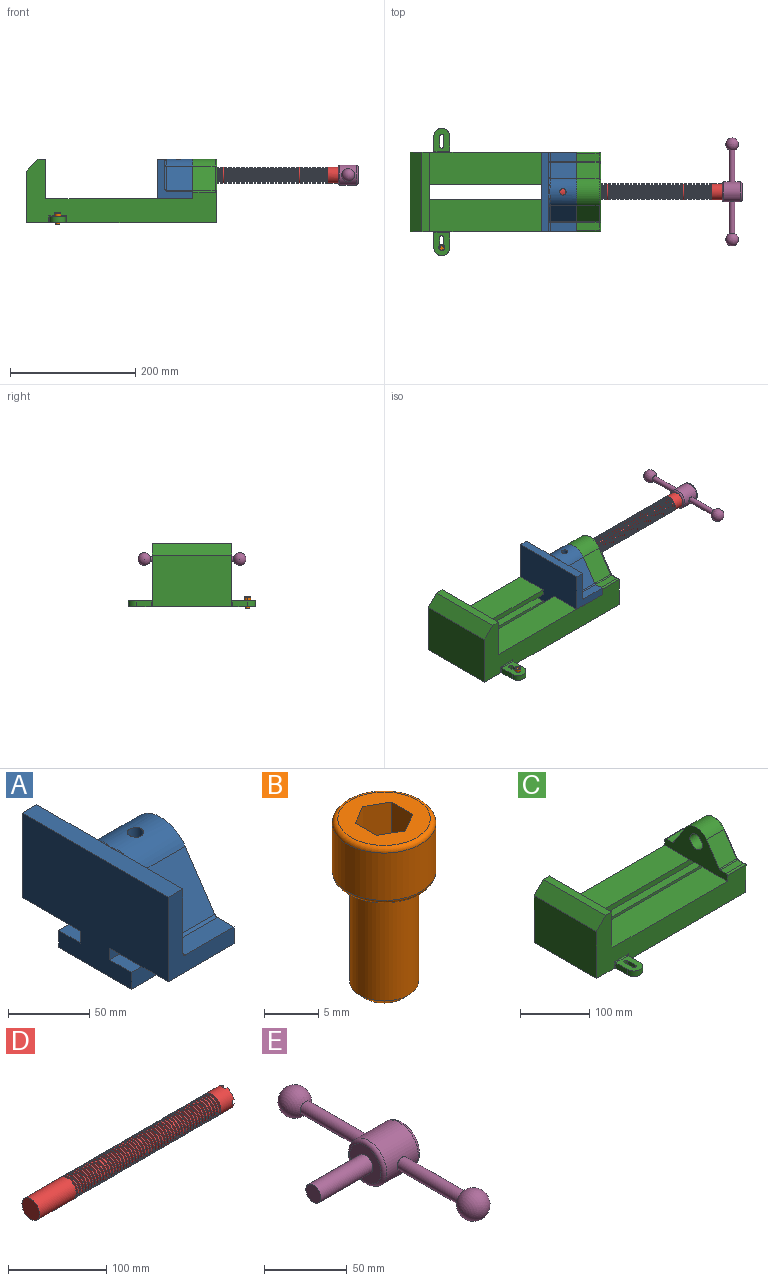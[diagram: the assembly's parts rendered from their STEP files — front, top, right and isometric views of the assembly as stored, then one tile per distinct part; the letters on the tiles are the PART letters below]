
ASSEMBLY  parts=5 mates=5
PART A: 36 faces, bbox 57.2x127x89 mm
  f0: plane 57.15x50.8mm, normal (0,0,-1), area 2903.2mm2, adj f6,f9,f10,f23
  f1: cylinder r=12.7mm len=44.45mm, axis (1,0,0), area 3464.3mm2, adj f6,f15,f16
  f2: plane 41.91x14.52mm, normal (0,0,1), area 608.5mm2, adj f6,f11,f24,f25
  f3: plane 51.86x48.26mm, normal (1,0,0), area 1495.7mm2, adj f8,f10,f31,f33,f35
  f4: plane 51.86x48.26mm, normal (1,0,0), area 1495.7mm2, adj f8,f11,f24,f28,f29
  f5: plane 57.15x50.8mm, normal (0,0,-1), area 2903.2mm2, adj f6,f9,f11,f22
  f6: plane 127x85.09mm, normal (1,0,0), area 5190.6mm2, adj f0,f1,f2,f5,f7,f10,f11,f12
  f7: plane 41.91x14.52mm, normal (0,0,1), area 608.5mm2, adj f6,f10,f30,f31
  f8: plane 127x12.7mm, normal (0,0,1), area 1612.9mm2, adj f3,f4,f9,f10,f11,f26,f34
  f9: plane 127x85.09mm, normal (-1,0,0), area 9096.8mm2, adj f0,f5,f8,f10,f11,f17,f18,f19
  f10: plane 63.5x57.15mm, normal (0,-1,0), area 1372.3mm2, adj f0,f3,f6,f7,f8,f9,f31
  f11: plane 63.5x57.15mm, normal (0,1,0), area 1372.3mm2, adj f2,f4,f5,f6,f8,f9,f24
  f12: plane 41.91x38.43mm, normal (0,-0.83,0.56), area 1939.2mm2, adj f6,f13,f30,f33
  f13: cylinder r=25.4mm len=44.45mm, axis (1,0,0), area 2026.5mm2, adj f6,f12,f14,f16,f26,f28,f34,f35
  f14: plane 41.91x38.43mm, normal (0,0.83,0.56), area 1939.2mm2, adj f6,f13,f25,f29
  f15: plane 25.4x25.4mm, normal (1,0,0), area 506.7mm2, adj f1
  f16: cylinder r=5.08mm len=13.76mm, axis (0,0,1), area 414mm2, adj f1,f13
  f17: plane 57.15x19.05mm, normal (0,0,1), area 1088.7mm2, adj f6,f9,f18,f23
  f18: plane 57.15x12.7mm, normal (0,-1,0), area 725.8mm2, adj f6,f9,f17,f19
  f19: plane 63.5x57.15mm, normal (0,0,-1), area 3629mm2, adj f6,f9,f18,f20
  f20: plane 57.15x12.7mm, normal (0,1,0), area 725.8mm2, adj f6,f9,f19,f21
  f21: plane 57.15x19.05mm, normal (0,0,1), area 1088.7mm2, adj f6,f9,f20,f22
  f22: plane 57.15x8.89mm, normal (0,1,0), area 508.1mm2, adj f5,f6,f9,f21
  f23: plane 57.15x8.89mm, normal (0,-1,0), area 508.1mm2, adj f0,f6,f9,f17
  f24: cylinder r=2.54mm len=14.52mm, axis (0,-1,0), area 57.9mm2, adj f2,f4,f11,f27
  f25: cylinder r=2.54mm len=41.91mm, axis (1,0,0), area 104.3mm2, adj f2,f6,f14,f27
  f26: bspline ~12.24x2.8mm, area 20.9mm2, adj f8,f13,f28
  f27: sphere r=2.54mm, area 6.3mm2, adj f24,f25,f29
  f28: torus R=27.94mm, axis (1,0,0), area 57.8mm2, adj f4,f13,f26,f29
  f29: cylinder r=2.54mm len=39.84mm, axis (0,-0.56,0.83), area 184.6mm2, adj f4,f14,f27,f28
  f30: cylinder r=2.54mm len=41.91mm, axis (1,0,0), area 104.3mm2, adj f6,f7,f12,f32
  f31: cylinder r=2.54mm len=14.52mm, axis (0,-1,0), area 57.9mm2, adj f3,f7,f10,f32
  f32: sphere r=2.54mm, area 6.3mm2, adj f30,f31,f33
  f33: cylinder r=2.54mm len=39.84mm, axis (0,-0.56,-0.83), area 184.6mm2, adj f3,f12,f32,f35
  f34: bspline ~12.24x2.8mm, area 20.9mm2, adj f8,f13,f35
  f35: torus R=27.94mm, axis (1,0,0), area 57.8mm2, adj f3,f13,f33,f34
PART B: 15 faces, bbox 10.3x10.3x19.1 mm
  f0: plane 8.51x8.51mm, normal (0,0,1), area 37.2mm2, adj f5,f6,f7,f8,f9,f10,f14
  f1: cylinder r=3.17mm len=11.94mm, axis (0,0,1), area 238.2mm2, adj f4,f12
  f2: plane 4.83x4.83mm, normal (0,0,-1), area 18.3mm2, adj f12
  f3: cylinder r=4.76mm len=9.53mm, axis (0,0,-1), area 159.6mm2, adj f13,f14
  f4: plane 8.51x8.51mm, normal (0,0,-1), area 25.2mm2, adj f1,f13
  f5: plane 4.83x2.38mm, normal (-0.5,-0.87,0), area 13.3mm2, adj f0,f6,f10,f11
  f6: plane 4.83x2.38mm, normal (0.5,-0.87,0), area 13.3mm2, adj f0,f5,f7,f11
  f7: plane 4.83x2.75mm, normal (1,0,0), area 13.3mm2, adj f0,f6,f8,f11
  f8: plane 4.83x2.38mm, normal (0.5,0.87,0), area 13.3mm2, adj f0,f7,f9,f11
  f9: plane 4.83x2.38mm, normal (-0.5,0.87,0), area 13.3mm2, adj f0,f8,f10,f11
  f10: plane 4.83x2.75mm, normal (-1,0,0), area 13.3mm2, adj f0,f5,f9,f11
  f11: plane 5.5x4.76mm, normal (0,0,1), area 19.6mm2, adj f5,f6,f7,f8,f9,f10
  f12: cone r=3.17mm half-angle=45deg, axis (0,0,1), area 18.9mm2, adj f1,f2
  f13: torus R=4.25mm, axis (0,0,1), area 23mm2, adj f3,f4
  f14: torus R=4.25mm, axis (0,0,1), area 23mm2, adj f0,f3
PART C: 61 faces, bbox 304.8x203.2x103.7 mm
  f0: plane 304.8x101.6mm, normal (0,1,0), area 13520.3mm2, adj f3,f4,f5,f6,f7,f8,f9,f16
  f1: plane 304.8x101.6mm, normal (0,-1,0), area 13520.3mm2, adj f2,f3,f5,f6,f7,f8,f9,f16
  f2: plane 234.95x50.8mm, normal (0,0,1), area 11935.5mm2, adj f1,f5,f16,f26
  f3: plane 127x99.06mm, normal (1,0,0), area 7097.5mm2, adj f0,f1,f9,f14,f17,f18,f19,f20
  f4: plane 234.95x50.8mm, normal (0,0,1), area 11935.5mm2, adj f0,f5,f16,f27
  f5: plane 127x101.6mm, normal (1,0,0), area 9516.1mm2, adj f0,f1,f2,f4,f6,f9,f18,f19
  f6: plane 127x12.7mm, normal (0,0,1), area 1612.9mm2, adj f0,f1,f5,f7
  f7: plane 127x19.05mm, normal (-0.71,0,0.71), area 3421.5mm2, adj f0,f1,f6,f8
  f8: plane 127x82.55mm, normal (-1,0,0), area 10483.8mm2, adj f0,f1,f7,f9
  f9: plane 304.8x203.2mm, normal (0,0,-1), area 33298.3mm2, adj f0,f1,f3,f5,f8,f21,f22,f39
  f10: plane 35.56x11.98mm, normal (0,0,1), area 426mm2, adj f16,f28,f29,f30
  f11: plane 38.43x35.56mm, normal (0,0.83,0.56), area 1645.4mm2, adj f12,f16,f29,f32
  f12: cylinder r=25.4mm len=42.19mm, axis (1,0,0), area 1770.2mm2, adj f11,f13,f16,f33
  f13: plane 38.43x35.56mm, normal (0,-0.83,0.56), area 1645.4mm2, adj f12,f16,f34,f35
  f14: cylinder r=12.7mm len=38.1mm, axis (1,0,0), area 3040.2mm2, adj f3,f16
  f15: plane 35.56x11.98mm, normal (0,0,1), area 426mm2, adj f16,f34,f36,f38
  f16: plane 127x63.5mm, normal (-1,0,0), area 4155.5mm2, adj f0,f1,f2,f4,f10,f11,f12,f13
  f17: plane 38.1x25.4mm, normal (0,0,-1), area 967.7mm2, adj f3,f16,f26,f27
  f18: plane 273.05x19.05mm, normal (0,0,-1), area 5201.6mm2, adj f3,f5,f19,f26
  f19: plane 273.05x12.7mm, normal (0,1,0), area 3467.7mm2, adj f3,f5,f18,f20
  f20: plane 273.05x19.05mm, normal (0,0,1), area 5201.6mm2, adj f3,f5,f19,f21
  f21: plane 273.05x16.51mm, normal (0,1,0), area 4508.1mm2, adj f3,f5,f9,f20
  f22: plane 273.05x16.51mm, normal (0,-1,0), area 4508.1mm2, adj f3,f5,f9,f23
  f23: plane 273.05x19.05mm, normal (0,0,1), area 5201.6mm2, adj f3,f5,f22,f24
  f24: plane 273.05x12.7mm, normal (0,-1,0), area 3467.7mm2, adj f3,f5,f23,f25
  f25: plane 273.05x19.05mm, normal (0,0,-1), area 5201.6mm2, adj f3,f5,f24,f27
  f26: plane 273.05x8.89mm, normal (0,1,0), area 2427.4mm2, adj f2,f3,f5,f17,f18
  f27: plane 273.05x8.89mm, normal (0,-1,0), area 2427.4mm2, adj f3,f4,f5,f17,f25
  f28: cylinder r=2.54mm len=38.1mm, axis (1,0,0), area 148.3mm2, adj f0,f10,f16,f30
  f29: cylinder r=2.54mm len=35.56mm, axis (-1,0,0), area 88.5mm2, adj f10,f11,f16,f31
  f30: cylinder r=2.54mm len=14.52mm, axis (0,1,0), area 54.3mm2, adj f3,f10,f28,f31
  f31: torus R=5.08mm, axis (-1,0,0), area 13.5mm2, adj f3,f29,f30,f32
  f32: cylinder r=2.54mm len=39.84mm, axis (0,0.56,-0.83), area 184.6mm2, adj f3,f11,f31,f33
  f33: torus R=22.86mm, axis (-1,0,0), area 191.4mm2, adj f3,f12,f32,f35
  f34: cylinder r=2.54mm len=35.56mm, axis (-1,0,0), area 88.5mm2, adj f13,f15,f16,f37
  f35: cylinder r=2.54mm len=39.84mm, axis (0,0.56,0.83), area 184.6mm2, adj f3,f13,f33,f37
  f36: cylinder r=2.54mm len=38.1mm, axis (-1,0,0), area 148.3mm2, adj f1,f15,f16,f38
  f37: torus R=5.08mm, axis (-1,0,0), area 13.5mm2, adj f3,f34,f35,f38
  f38: cylinder r=2.54mm len=14.52mm, axis (0,1,0), area 54.3mm2, adj f3,f15,f36,f37
  f39: plane 23.88x9.53mm, normal (-1,0,0), area 227.4mm2, adj f9,f45,f46,f60
  f40: plane 23.88x9.53mm, normal (1,0,0), area 227.4mm2, adj f9,f45,f46,f58
  f41: cylinder r=3.3mm len=9.53mm, axis (0,0,-1), area 98.8mm2, adj f9,f42,f44,f46
  f42: plane 15.62x9.53mm, normal (-1,0,0), area 148.8mm2, adj f9,f41,f43,f46
  f43: cylinder r=3.3mm len=9.53mm, axis (0,0,-1), area 98.8mm2, adj f9,f42,f44,f46
  f44: plane 15.62x9.53mm, normal (1,0,0), area 148.8mm2, adj f9,f41,f43,f46
  f45: cylinder r=12.7mm len=25.4mm, axis (0,0,-1), area 380mm2, adj f9,f39,f40,f46
  f46: plane 36.58x25.4mm, normal (0,0,1), area 722.4mm2, adj f39,f40,f41,f42,f43,f44,f45,f59
  f47: plane 23.88x9.53mm, normal (-1,0,0), area 227.4mm2, adj f9,f53,f54,f56
  f48: plane 23.88x9.53mm, normal (1,0,0), area 227.4mm2, adj f9,f53,f54,f55
  f49: cylinder r=3.3mm len=9.53mm, axis (0,0,-1), area 98.8mm2, adj f9,f50,f52,f54
  f50: plane 15.62x9.53mm, normal (-1,0,0), area 148.8mm2, adj f9,f49,f51,f54
  f51: cylinder r=3.3mm len=9.53mm, axis (0,0,-1), area 98.8mm2, adj f9,f50,f52,f54
  f52: plane 15.62x9.53mm, normal (1,0,0), area 148.8mm2, adj f9,f49,f51,f54
  f53: cylinder r=12.7mm len=25.4mm, axis (0,0,-1), area 380mm2, adj f9,f47,f48,f54
  f54: plane 36.58x25.4mm, normal (0,0,1), area 722.4mm2, adj f47,f48,f49,f50,f51,f52,f53,f57
  f55: cylinder r=1.52mm len=11.05mm, axis (0,0,-1), area 24.1mm2, adj f0,f9,f48,f57
  f56: cylinder r=1.52mm len=11.05mm, axis (0,0,1), area 24.1mm2, adj f0,f9,f47,f57
  f57: cylinder r=1.52mm len=28.45mm, axis (1,0,0), area 63.5mm2, adj f0,f54,f55,f56
  f58: cylinder r=1.52mm len=11.05mm, axis (0,0,1), area 24.1mm2, adj f1,f9,f40,f59
  f59: cylinder r=1.52mm len=28.45mm, axis (-1,0,0), area 63.5mm2, adj f1,f46,f58,f60
  f60: cylinder r=1.52mm len=11.05mm, axis (0,0,-1), area 24.1mm2, adj f1,f9,f39,f59
PART D: 220 faces, bbox 279.4x25.4x25.4 mm
  f0: cylinder r=12.7mm len=25.4mm, axis (-1,0,0), area 1468.2mm2, adj f1,f2,f3,f5,f7,f208,f209,f210
  f1: plane 9.9x9.9mm, normal (1,0,0), area 62.3mm2, adj f0,f4,f213,f216
  f2: plane 9.9x9.9mm, normal (1,0,0), area 62.3mm2, adj f0,f4,f210,f218
  f3: plane 9.9x9.9mm, normal (1,0,0), area 62.3mm2, adj f0,f4,f209,f212
  f4: cylinder r=6.35mm len=25.4mm, axis (1,0,0), area 960.3mm2, adj f1,f2,f3,f5,f6,f208,f209,f210
  f5: plane 9.9x9.9mm, normal (1,0,0), area 62.3mm2, adj f0,f4,f215,f217
  f6: plane 12.7x12.7mm, normal (1,0,0), area 126.7mm2, adj f4
  f7: cone r=12.7mm half-angle=76deg, axis (1,0,0), area 188mm2, adj f0,f9
  f8: cone r=10.16mm half-angle=76deg, axis (-1,0,0), area 188mm2, adj f9,f10
  f9: cylinder r=10.16mm len=20.32mm, axis (1,0,0), area 81.1mm2, adj f7,f8
  f10: cylinder r=12.7mm len=25.4mm, axis (-1,0,0), area 131.7mm2, adj f8,f11
  f11: cone r=12.7mm half-angle=76deg, axis (1,0,0), area 188mm2, adj f10,f13
  f12: cone r=10.16mm half-angle=76deg, axis (-1,0,0), area 188mm2, adj f13,f14
  f13: cylinder r=10.16mm len=20.32mm, axis (1,0,0), area 81.1mm2, adj f11,f12
  f14: cylinder r=12.7mm len=25.4mm, axis (-1,0,0), area 131.7mm2, adj f12,f15
  f15: cone r=12.7mm half-angle=76deg, axis (1,0,0), area 188mm2, adj f14,f17
  f16: cone r=10.16mm half-angle=76deg, axis (-1,0,0), area 188mm2, adj f17,f18
  f17: cylinder r=10.16mm len=20.32mm, axis (1,0,0), area 81.1mm2, adj f15,f16
  f18: cylinder r=12.7mm len=25.4mm, axis (-1,0,0), area 131.7mm2, adj f16,f19
  f19: cone r=12.7mm half-angle=76deg, axis (1,0,0), area 188mm2, adj f18,f21
  f20: cone r=10.16mm half-angle=76deg, axis (-1,0,0), area 188mm2, adj f21,f22
  f21: cylinder r=10.16mm len=20.32mm, axis (1,0,0), area 81.1mm2, adj f19,f20
  f22: cylinder r=12.7mm len=25.4mm, axis (-1,0,0), area 131.7mm2, adj f20,f23
  f23: cone r=12.7mm half-angle=76deg, axis (1,0,0), area 188mm2, adj f22,f25
  f24: cone r=10.16mm half-angle=76deg, axis (-1,0,0), area 188mm2, adj f25,f26
  f25: cylinder r=10.16mm len=20.32mm, axis (1,0,0), area 81.1mm2, adj f23,f24
  f26: cylinder r=12.7mm len=25.4mm, axis (-1,0,0), area 131.7mm2, adj f24,f27
  f27: cone r=12.7mm half-angle=76deg, axis (1,0,0), area 188mm2, adj f26,f29
  f28: cone r=10.16mm half-angle=76deg, axis (-1,0,0), area 188mm2, adj f29,f30
  f29: cylinder r=10.16mm len=20.32mm, axis (1,0,0), area 81.1mm2, adj f27,f28
  f30: cylinder r=12.7mm len=25.4mm, axis (-1,0,0), area 131.7mm2, adj f28,f31
  f31: cone r=12.7mm half-angle=76deg, axis (1,0,0), area 188mm2, adj f30,f33
  f32: cone r=10.16mm half-angle=76deg, axis (-1,0,0), area 188mm2, adj f33,f34
  f33: cylinder r=10.16mm len=20.32mm, axis (1,0,0), area 81.1mm2, adj f31,f32
  f34: cylinder r=12.7mm len=25.4mm, axis (-1,0,0), area 131.7mm2, adj f32,f35
  f35: cone r=12.7mm half-angle=76deg, axis (1,0,0), area 188mm2, adj f34,f37
  f36: cone r=10.16mm half-angle=76deg, axis (-1,0,0), area 188mm2, adj f37,f38
  f37: cylinder r=10.16mm len=20.32mm, axis (1,0,0), area 81.1mm2, adj f35,f36
  f38: cylinder r=12.7mm len=25.4mm, axis (-1,0,0), area 131.7mm2, adj f36,f39
  f39: cone r=12.7mm half-angle=76deg, axis (1,0,0), area 188mm2, adj f38,f41
  f40: cone r=10.16mm half-angle=76deg, axis (-1,0,0), area 188mm2, adj f41,f42
  f41: cylinder r=10.16mm len=20.32mm, axis (1,0,0), area 81.1mm2, adj f39,f40
  f42: cylinder r=12.7mm len=25.4mm, axis (-1,0,0), area 131.7mm2, adj f40,f43
  f43: cone r=12.7mm half-angle=76deg, axis (1,0,0), area 188mm2, adj f42,f45
  f44: cone r=10.16mm half-angle=76deg, axis (-1,0,0), area 188mm2, adj f45,f46
  f45: cylinder r=10.16mm len=20.32mm, axis (1,0,0), area 81.1mm2, adj f43,f44
  f46: cylinder r=12.7mm len=25.4mm, axis (-1,0,0), area 131.7mm2, adj f44,f47
  f47: cone r=12.7mm half-angle=76deg, axis (1,0,0), area 188mm2, adj f46,f49
  f48: cone r=10.16mm half-angle=76deg, axis (-1,0,0), area 188mm2, adj f49,f50
  f49: cylinder r=10.16mm len=20.32mm, axis (1,0,0), area 81.1mm2, adj f47,f48
  f50: cylinder r=12.7mm len=25.4mm, axis (-1,0,0), area 131.7mm2, adj f48,f51
  f51: cone r=12.7mm half-angle=76deg, axis (1,0,0), area 188mm2, adj f50,f53
  f52: cone r=10.16mm half-angle=76deg, axis (-1,0,0), area 188mm2, adj f53,f54
  f53: cylinder r=10.16mm len=20.32mm, axis (1,0,0), area 81.1mm2, adj f51,f52
  f54: cylinder r=12.7mm len=25.4mm, axis (-1,0,0), area 131.7mm2, adj f52,f55
  f55: cone r=12.7mm half-angle=76deg, axis (1,0,0), area 188mm2, adj f54,f57
  f56: cone r=10.16mm half-angle=76deg, axis (-1,0,0), area 188mm2, adj f57,f58
  f57: cylinder r=10.16mm len=20.32mm, axis (1,0,0), area 81.1mm2, adj f55,f56
  f58: cylinder r=12.7mm len=25.4mm, axis (-1,0,0), area 131.7mm2, adj f56,f59
  f59: cone r=12.7mm half-angle=76deg, axis (1,0,0), area 188mm2, adj f58,f61
  f60: cone r=10.16mm half-angle=76deg, axis (-1,0,0), area 188mm2, adj f61,f62
  f61: cylinder r=10.16mm len=20.32mm, axis (1,0,0), area 81.1mm2, adj f59,f60
  f62: cylinder r=12.7mm len=25.4mm, axis (-1,0,0), area 131.7mm2, adj f60,f63
  f63: cone r=12.7mm half-angle=76deg, axis (1,0,0), area 188mm2, adj f62,f65
  f64: cone r=10.16mm half-angle=76deg, axis (-1,0,0), area 188mm2, adj f65,f66
  f65: cylinder r=10.16mm len=20.32mm, axis (1,0,0), area 81.1mm2, adj f63,f64
  f66: cylinder r=12.7mm len=25.4mm, axis (-1,0,0), area 131.7mm2, adj f64,f67
  f67: cone r=12.7mm half-angle=76deg, axis (1,0,0), area 188mm2, adj f66,f69
  f68: cone r=10.16mm half-angle=76deg, axis (-1,0,0), area 188mm2, adj f69,f70
  f69: cylinder r=10.16mm len=20.32mm, axis (1,0,0), area 81.1mm2, adj f67,f68
  f70: cylinder r=12.7mm len=25.4mm, axis (-1,0,0), area 131.7mm2, adj f68,f71
  f71: cone r=12.7mm half-angle=76deg, axis (1,0,0), area 188mm2, adj f70,f73
  f72: cone r=10.16mm half-angle=76deg, axis (-1,0,0), area 188mm2, adj f73,f74
  f73: cylinder r=10.16mm len=20.32mm, axis (1,0,0), area 81.1mm2, adj f71,f72
  f74: cylinder r=12.7mm len=25.4mm, axis (-1,0,0), area 131.7mm2, adj f72,f75
  f75: cone r=12.7mm half-angle=76deg, axis (1,0,0), area 188mm2, adj f74,f77
  f76: cone r=10.16mm half-angle=76deg, axis (-1,0,0), area 188mm2, adj f77,f78
  f77: cylinder r=10.16mm len=20.32mm, axis (1,0,0), area 81.1mm2, adj f75,f76
  f78: cylinder r=12.7mm len=25.4mm, axis (-1,0,0), area 131.7mm2, adj f76,f79
  f79: cone r=12.7mm half-angle=76deg, axis (1,0,0), area 188mm2, adj f78,f81
  f80: cone r=10.16mm half-angle=76deg, axis (-1,0,0), area 188mm2, adj f81,f82
  f81: cylinder r=10.16mm len=20.32mm, axis (1,0,0), area 81.1mm2, adj f79,f80
  f82: cylinder r=12.7mm len=25.4mm, axis (-1,0,0), area 131.7mm2, adj f80,f83
  f83: cone r=12.7mm half-angle=76deg, axis (1,0,0), area 188mm2, adj f82,f85
  f84: cone r=10.16mm half-angle=76deg, axis (-1,0,0), area 188mm2, adj f85,f86
  f85: cylinder r=10.16mm len=20.32mm, axis (1,0,0), area 81.1mm2, adj f83,f84
  f86: cylinder r=12.7mm len=25.4mm, axis (-1,0,0), area 131.7mm2, adj f84,f87
  f87: cone r=12.7mm half-angle=76deg, axis (1,0,0), area 188mm2, adj f86,f89
  f88: cone r=10.16mm half-angle=76deg, axis (-1,0,0), area 188mm2, adj f89,f90
  f89: cylinder r=10.16mm len=20.32mm, axis (1,0,0), area 81.1mm2, adj f87,f88
  f90: cylinder r=12.7mm len=25.4mm, axis (-1,0,0), area 131.7mm2, adj f88,f91
  f91: cone r=12.7mm half-angle=76deg, axis (1,0,0), area 188mm2, adj f90,f93
  f92: cone r=10.16mm half-angle=76deg, axis (-1,0,0), area 188mm2, adj f93,f94
  f93: cylinder r=10.16mm len=20.32mm, axis (1,0,0), area 81.1mm2, adj f91,f92
  f94: cylinder r=12.7mm len=25.4mm, axis (-1,0,0), area 131.7mm2, adj f92,f95
  f95: cone r=12.7mm half-angle=76deg, axis (1,0,0), area 188mm2, adj f94,f97
  f96: cone r=10.16mm half-angle=76deg, axis (-1,0,0), area 188mm2, adj f97,f98
  f97: cylinder r=10.16mm len=20.32mm, axis (1,0,0), area 81.1mm2, adj f95,f96
  f98: cylinder r=12.7mm len=25.4mm, axis (-1,0,0), area 131.7mm2, adj f96,f99
  f99: cone r=12.7mm half-angle=76deg, axis (1,0,0), area 188mm2, adj f98,f101
  f100: cone r=10.16mm half-angle=76deg, axis (-1,0,0), area 188mm2, adj f101,f102
  f101: cylinder r=10.16mm len=20.32mm, axis (1,0,0), area 81.1mm2, adj f99,f100
  f102: cylinder r=12.7mm len=25.4mm, axis (-1,0,0), area 131.7mm2, adj f100,f103
  f103: cone r=12.7mm half-angle=76deg, axis (1,0,0), area 188mm2, adj f102,f105
  f104: cone r=10.16mm half-angle=76deg, axis (-1,0,0), area 188mm2, adj f105,f106
  f105: cylinder r=10.16mm len=20.32mm, axis (1,0,0), area 81.1mm2, adj f103,f104
  f106: cylinder r=12.7mm len=25.4mm, axis (-1,0,0), area 131.7mm2, adj f104,f107
  f107: cone r=12.7mm half-angle=76deg, axis (1,0,0), area 188mm2, adj f106,f109
  f108: cone r=10.16mm half-angle=76deg, axis (-1,0,0), area 188mm2, adj f109,f110
  f109: cylinder r=10.16mm len=20.32mm, axis (1,0,0), area 81.1mm2, adj f107,f108
  f110: cylinder r=12.7mm len=25.4mm, axis (-1,0,0), area 131.7mm2, adj f108,f111
  f111: cone r=12.7mm half-angle=76deg, axis (1,0,0), area 188mm2, adj f110,f113
  f112: cone r=10.16mm half-angle=76deg, axis (-1,0,0), area 188mm2, adj f113,f114
  f113: cylinder r=10.16mm len=20.32mm, axis (1,0,0), area 81.1mm2, adj f111,f112
  f114: cylinder r=12.7mm len=25.4mm, axis (-1,0,0), area 131.7mm2, adj f112,f115
  f115: cone r=12.7mm half-angle=76deg, axis (1,0,0), area 188mm2, adj f114,f117
  f116: cone r=10.16mm half-angle=76deg, axis (-1,0,0), area 188mm2, adj f117,f118
  f117: cylinder r=10.16mm len=20.32mm, axis (1,0,0), area 81.1mm2, adj f115,f116
  f118: cylinder r=12.7mm len=25.4mm, axis (-1,0,0), area 131.7mm2, adj f116,f119
  f119: cone r=12.7mm half-angle=76deg, axis (1,0,0), area 188mm2, adj f118,f121
  f120: cone r=10.16mm half-angle=76deg, axis (-1,0,0), area 188mm2, adj f121,f122
  f121: cylinder r=10.16mm len=20.32mm, axis (1,0,0), area 81.1mm2, adj f119,f120
  f122: cylinder r=12.7mm len=25.4mm, axis (-1,0,0), area 131.7mm2, adj f120,f123
  f123: cone r=12.7mm half-angle=76deg, axis (1,0,0), area 188mm2, adj f122,f125
  f124: cone r=10.16mm half-angle=76deg, axis (-1,0,0), area 188mm2, adj f125,f126
  f125: cylinder r=10.16mm len=20.32mm, axis (1,0,0), area 81.1mm2, adj f123,f124
  f126: cylinder r=12.7mm len=25.4mm, axis (-1,0,0), area 131.7mm2, adj f124,f127
  f127: cone r=12.7mm half-angle=76deg, axis (1,0,0), area 188mm2, adj f126,f129
  f128: cone r=10.16mm half-angle=76deg, axis (-1,0,0), area 188mm2, adj f129,f130
  f129: cylinder r=10.16mm len=20.32mm, axis (1,0,0), area 81.1mm2, adj f127,f128
  f130: cylinder r=12.7mm len=25.4mm, axis (-1,0,0), area 131.7mm2, adj f128,f131
  f131: cone r=12.7mm half-angle=76deg, axis (1,0,0), area 188mm2, adj f130,f133
  f132: cone r=10.16mm half-angle=76deg, axis (-1,0,0), area 188mm2, adj f133,f134
  f133: cylinder r=10.16mm len=20.32mm, axis (1,0,0), area 81.1mm2, adj f131,f132
  f134: cylinder r=12.7mm len=25.4mm, axis (-1,0,0), area 131.7mm2, adj f132,f135
  f135: cone r=12.7mm half-angle=76deg, axis (1,0,0), area 188mm2, adj f134,f137
  f136: cone r=10.16mm half-angle=76deg, axis (-1,0,0), area 188mm2, adj f137,f138
  f137: cylinder r=10.16mm len=20.32mm, axis (1,0,0), area 81.1mm2, adj f135,f136
  f138: cylinder r=12.7mm len=25.4mm, axis (-1,0,0), area 131.7mm2, adj f136,f139
  f139: cone r=12.7mm half-angle=76deg, axis (1,0,0), area 188mm2, adj f138,f141
  f140: cone r=10.16mm half-angle=76deg, axis (-1,0,0), area 188mm2, adj f141,f142
  f141: cylinder r=10.16mm len=20.32mm, axis (1,0,0), area 81.1mm2, adj f139,f140
  f142: cylinder r=12.7mm len=25.4mm, axis (-1,0,0), area 131.7mm2, adj f140,f143
  f143: cone r=12.7mm half-angle=76deg, axis (1,0,0), area 188mm2, adj f142,f145
  f144: cone r=10.16mm half-angle=76deg, axis (-1,0,0), area 188mm2, adj f145,f146
  f145: cylinder r=10.16mm len=20.32mm, axis (1,0,0), area 81.1mm2, adj f143,f144
  f146: cylinder r=12.7mm len=25.4mm, axis (-1,0,0), area 131.7mm2, adj f144,f147
  f147: cone r=12.7mm half-angle=76deg, axis (1,0,0), area 188mm2, adj f146,f149
  f148: cone r=10.16mm half-angle=76deg, axis (-1,0,0), area 188mm2, adj f149,f150
  f149: cylinder r=10.16mm len=20.32mm, axis (1,0,0), area 81.1mm2, adj f147,f148
  f150: cylinder r=12.7mm len=25.4mm, axis (-1,0,0), area 131.7mm2, adj f148,f151
  f151: cone r=12.7mm half-angle=76deg, axis (1,0,0), area 188mm2, adj f150,f153
  f152: cone r=10.16mm half-angle=76deg, axis (-1,0,0), area 188mm2, adj f153,f154
  f153: cylinder r=10.16mm len=20.32mm, axis (1,0,0), area 81.1mm2, adj f151,f152
  f154: cylinder r=12.7mm len=25.4mm, axis (-1,0,0), area 131.7mm2, adj f152,f155
  f155: cone r=12.7mm half-angle=76deg, axis (1,0,0), area 188mm2, adj f154,f157
  f156: cone r=10.16mm half-angle=76deg, axis (-1,0,0), area 188mm2, adj f157,f158
  f157: cylinder r=10.16mm len=20.32mm, axis (1,0,0), area 81.1mm2, adj f155,f156
  f158: cylinder r=12.7mm len=25.4mm, axis (-1,0,0), area 131.7mm2, adj f156,f159
  f159: cone r=12.7mm half-angle=76deg, axis (1,0,0), area 188mm2, adj f158,f161
  f160: cone r=10.16mm half-angle=76deg, axis (-1,0,0), area 188mm2, adj f161,f162
  f161: cylinder r=10.16mm len=20.32mm, axis (1,0,0), area 81.1mm2, adj f159,f160
  f162: cylinder r=12.7mm len=25.4mm, axis (-1,0,0), area 131.7mm2, adj f160,f163
  f163: cone r=12.7mm half-angle=76deg, axis (1,0,0), area 188mm2, adj f162,f165
  f164: cone r=10.16mm half-angle=76deg, axis (-1,0,0), area 188mm2, adj f165,f166
  f165: cylinder r=10.16mm len=20.32mm, axis (1,0,0), area 81.1mm2, adj f163,f164
  f166: cylinder r=12.7mm len=25.4mm, axis (-1,0,0), area 131.7mm2, adj f164,f167
  f167: cone r=12.7mm half-angle=76deg, axis (1,0,0), area 188mm2, adj f166,f169
  f168: cone r=10.16mm half-angle=76deg, axis (-1,0,0), area 188mm2, adj f169,f170
  f169: cylinder r=10.16mm len=20.32mm, axis (1,0,0), area 81.1mm2, adj f167,f168
  f170: cylinder r=12.7mm len=25.4mm, axis (-1,0,0), area 131.7mm2, adj f168,f171
  f171: cone r=12.7mm half-angle=76deg, axis (1,0,0), area 188mm2, adj f170,f173
  f172: cone r=10.16mm half-angle=76deg, axis (-1,0,0), area 188mm2, adj f173,f174
  f173: cylinder r=10.16mm len=20.32mm, axis (1,0,0), area 81.1mm2, adj f171,f172
  f174: cylinder r=12.7mm len=25.4mm, axis (-1,0,0), area 131.7mm2, adj f172,f175
  f175: cone r=12.7mm half-angle=76deg, axis (1,0,0), area 188mm2, adj f174,f177
  f176: cone r=10.16mm half-angle=76deg, axis (-1,0,0), area 188mm2, adj f177,f178
  f177: cylinder r=10.16mm len=20.32mm, axis (1,0,0), area 81.1mm2, adj f175,f176
  f178: cylinder r=12.7mm len=25.4mm, axis (-1,0,0), area 131.7mm2, adj f176,f179
  f179: cone r=12.7mm half-angle=76deg, axis (1,0,0), area 188mm2, adj f178,f181
  f180: cone r=10.16mm half-angle=76deg, axis (-1,0,0), area 188mm2, adj f181,f182
  f181: cylinder r=10.16mm len=20.32mm, axis (1,0,0), area 81.1mm2, adj f179,f180
  f182: cylinder r=12.7mm len=25.4mm, axis (-1,0,0), area 131.7mm2, adj f180,f183
  f183: cone r=12.7mm half-angle=76deg, axis (1,0,0), area 188mm2, adj f182,f185
  f184: cone r=10.16mm half-angle=76deg, axis (-1,0,0), area 188mm2, adj f185,f186
  f185: cylinder r=10.16mm len=20.32mm, axis (1,0,0), area 81.1mm2, adj f183,f184
  f186: cylinder r=12.7mm len=25.4mm, axis (-1,0,0), area 131.7mm2, adj f184,f187
  f187: cone r=12.7mm half-angle=76deg, axis (1,0,0), area 188mm2, adj f186,f189
  f188: cone r=10.16mm half-angle=76deg, axis (-1,0,0), area 188mm2, adj f189,f190
  f189: cylinder r=10.16mm len=20.32mm, axis (1,0,0), area 81.1mm2, adj f187,f188
  f190: cylinder r=12.7mm len=25.4mm, axis (-1,0,0), area 131.7mm2, adj f188,f191
  f191: cone r=12.7mm half-angle=76deg, axis (1,0,0), area 188mm2, adj f190,f193
  f192: cone r=10.16mm half-angle=76deg, axis (-1,0,0), area 188mm2, adj f193,f194
  f193: cylinder r=10.16mm len=20.32mm, axis (1,0,0), area 81.1mm2, adj f191,f192
  f194: cylinder r=12.7mm len=25.4mm, axis (-1,0,0), area 131.7mm2, adj f192,f195
  f195: cone r=12.7mm half-angle=76deg, axis (1,0,0), area 188mm2, adj f194,f197
  f196: cone r=10.16mm half-angle=76deg, axis (-1,0,0), area 188mm2, adj f197,f198
  f197: cylinder r=10.16mm len=20.32mm, axis (1,0,0), area 81.1mm2, adj f195,f196
  f198: cylinder r=12.7mm len=25.4mm, axis (-1,0,0), area 131.7mm2, adj f196,f199
  f199: cone r=12.7mm half-angle=76deg, axis (1,0,0), area 188mm2, adj f198,f201
  f200: cone r=10.16mm half-angle=76deg, axis (-1,0,0), area 188mm2, adj f201,f202
  f201: cylinder r=10.16mm len=20.32mm, axis (1,0,0), area 81.1mm2, adj f199,f200
  f202: cylinder r=12.7mm len=25.4mm, axis (-1,0,0), area 131.7mm2, adj f200,f203
  f203: cone r=12.7mm half-angle=76deg, axis (1,0,0), area 188mm2, adj f202,f205
  f204: cone r=10.16mm half-angle=76deg, axis (-1,0,0), area 188mm2, adj f205,f207
  f205: cylinder r=10.16mm len=20.32mm, axis (1,0,0), area 81.1mm2, adj f203,f204
  f206: plane 25.4x25.4mm, normal (-1,0,0), area 506.7mm2, adj f207
  f207: cylinder r=12.7mm len=52.45mm, axis (-1,0,0), area 4185.4mm2, adj f204,f206
  f208: plane 6.88x5.08mm, normal (1,0,0), area 32.7mm2, adj f0,f4,f209,f210
  f209: plane 6.62x2.54mm, normal (0,-1,0), area 16.8mm2, adj f0,f3,f4,f208
  f210: plane 6.62x2.54mm, normal (0,1,0), area 16.8mm2, adj f0,f2,f4,f208
  f211: plane 6.88x5.08mm, normal (1,0,0), area 32.7mm2, adj f0,f4,f212,f213
  f212: plane 6.62x2.54mm, normal (0,0,1), area 16.8mm2, adj f0,f3,f4,f211
  f213: plane 6.62x2.54mm, normal (0,0,-1), area 16.8mm2, adj f0,f1,f4,f211
  f214: plane 6.88x5.08mm, normal (1,0,0), area 32.7mm2, adj f0,f4,f215,f216
  f215: plane 6.62x2.54mm, normal (0,1,0), area 16.8mm2, adj f0,f4,f5,f214
  f216: plane 6.62x2.54mm, normal (0,-1,0), area 16.8mm2, adj f0,f1,f4,f214
  f217: plane 6.62x2.54mm, normal (0,0,-1), area 16.8mm2, adj f0,f4,f5,f219
  f218: plane 6.62x2.54mm, normal (0,0,1), area 16.8mm2, adj f0,f2,f4,f219
  f219: plane 6.88x5.08mm, normal (1,0,0), area 32.7mm2, adj f0,f4,f217,f218
PART E: 11 faces, bbox 76.2x172.7x34.4 mm
  f0: sphere r=10.16mm, area 1231.8mm2, adj f1
  f1: cylinder r=4.45mm len=51.82mm, axis (0,1,0), area 1438.5mm2, adj f0,f4
  f2: sphere r=10.16mm, area 1231.8mm2, adj f3
  f3: cylinder r=4.45mm len=51.82mm, axis (0,1,0), area 1438.5mm2, adj f2,f4
  f4: cylinder r=15.88mm len=31.75mm, axis (-1,0,0), area 2534.7mm2, adj f1,f3,f9,f10
  f5: cylinder r=6.35mm len=44.45mm, axis (-1,0,0), area 1773.5mm2, adj f6,f8
  f6: plane 12.7x12.7mm, normal (-1,0,0), area 126.7mm2, adj f5
  f7: plane 26.67x26.67mm, normal (1,0,0), area 558.6mm2, adj f10
  f8: plane 26.67x26.67mm, normal (-1,0,0), area 432mm2, adj f5,f9
  f9: torus R=13.33mm, axis (1,0,0), area 374.8mm2, adj f4,f8
  f10: torus R=13.33mm, axis (1,0,0), area 374.8mm2, adj f4,f7
PLACE A t=(177.8,0,0)mm
PLACE B rot(axis=(0,0,1),90deg) t=(-254,-88.9,9.52)mm
PLACE C at identity fixed
PLACE D rot(axis=(1,0,0),180deg) t=(177.8,0,152.4)mm
PLACE E rot(axis=(1,0,0),180deg) t=(156.21,0,152.4)mm
MATE fastened D.f4 <-> E.f5  axis (1,0,0) through (194.31,0,76.2)mm
MATE planar A.f0 <-> C.f2  axis (0,0,-1) through (-66.68,-38.1,38.1)mm
MATE pin_slot B.f1 <-> C.f41  axis (0,0,1) through (-254,-88.9,9.52)mm
MATE revolute D.f7 <-> A.f28  axis (-1,0,0) through (-82.55,0,76.2)mm
MATE cylindrical C.f12 <-> D.f7  axis (-1,0,0) through (-38.1,0,76.2)mm
